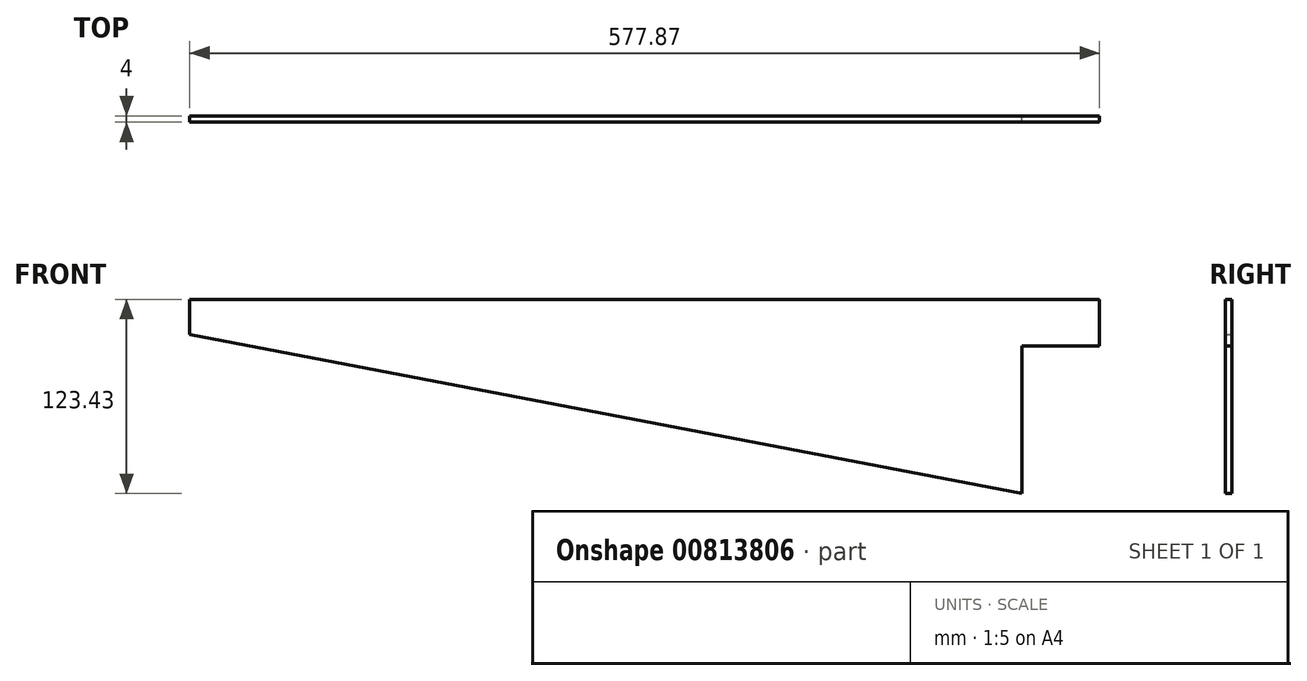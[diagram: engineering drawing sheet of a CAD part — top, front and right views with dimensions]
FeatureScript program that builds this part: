
annotation { "Feature Type Name" : "Feature", "Feature Type Description" : "" }
export const myFeature = defineFeature(function(context is Context, id is Id, definition is map)
    precondition{}
    {
        {
            var Q0;
            Q0=qCreatedBy(makeId("Front.planeOp"),FACE);
            var sketch = newSketch(context, id + "F0", { "sketchPlane" : qUnion([Q0])});
            skLineSegment(sketch, "E0", {"start": v(-323.95, 54.92) * mm, "end": v(253.92, 54.92) * mm});
            skLineSegment(sketch, "E1", {"start": v(253.92, 54.92) * mm, "end": v(253.92, 25.14) * mm});
            skLineSegment(sketch, "E2", {"start": v(253.92, 25.14) * mm, "end": v(204.72, 25.14) * mm});
            skLineSegment(sketch, "E3", {"start": v(204.72, 25.14) * mm, "end": v(204.72, -68.5) * mm});
            skLineSegment(sketch, "E4", {"start": v(204.72, -68.5) * mm, "end": v(-323.95, 32.48) * mm});
            skLineSegment(sketch, "E5", {"start": v(-323.95, 32.48) * mm, "end": v(-323.95, 54.92) * mm});
            skSolve(sketch);
        }
        {
            var Q0;
            Q0 = qSketchRegion(id + "F0", true);
            extrude(context, id + "F1", {"entities" : qUnion([Q0]), "depth" : 4 * mm, "offsetDistance" : 25 * mm});
        }
    });
